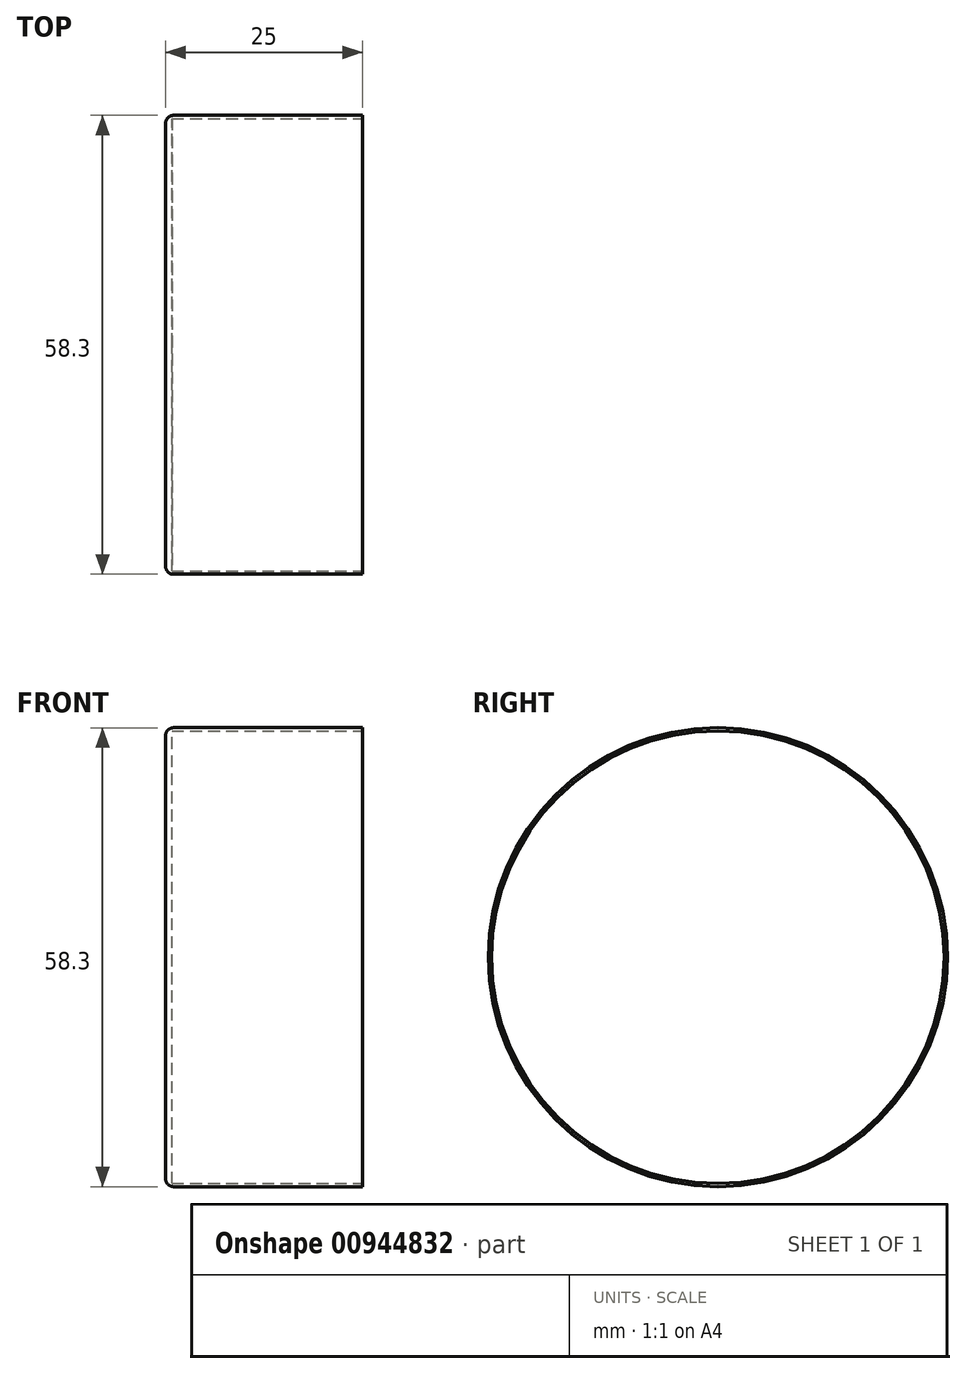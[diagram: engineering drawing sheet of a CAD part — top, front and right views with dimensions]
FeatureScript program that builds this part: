
annotation { "Feature Type Name" : "Feature", "Feature Type Description" : "" }
export const myFeature = defineFeature(function(context is Context, id is Id, definition is map)
    precondition{}
    {
        {
            var Q0;
            Q0=qCreatedBy(makeId("Front.planeOp"),FACE);
            var sketch = newSketch(context, id + "F0", { "sketchPlane" : qUnion([Q0])});
            skLineSegment(sketch, "E0", {"start": v(-31.94, -19.42) * mm, "end": v(-7.94, -19.42) * mm});
            skLineSegment(sketch, "E1", {"start": v(-7.94, -19.42) * mm, "end": v(-7.94, -19.02) * mm});
            skLineSegment(sketch, "E2", {"start": v(-7.94, -19.02) * mm, "end": v(-32.14, -19.02) * mm});
            skLineSegment(sketch, "E3", {"start": v(-32.14, -19.02) * mm, "end": v(-32.14, 9.73) * mm});
            skLineSegment(sketch, "E4", {"start": v(-32.14, 9.73) * mm, "end": v(-32.94, 9.73) * mm});
            skLineSegment(sketch, "E5", {"start": v(-32.94, 9.73) * mm, "end": v(-32.94, -18.42) * mm});
            skPoint(sketch, "E6.visualSharp", {"position": v(-32.94, -19.42) * mm});
            skArc(sketch, "E6.filletArc", {"start": v(-32.94, -18.42) * mm, "mid": v(-32.65, -19.12) * mm, "end": v(-31.94, -19.42) * mm});
            skSolve(sketch);
        }
        {
            var Q0;
            Q0 = qSketchRegion(id + "F0", true);
            var Q1;
            Q1=sQuery(id+"F0.wireOp",EDGE,"E4");
            revolve(context, id + "F1", {"surfaceOperationType" : NewSurfaceOperationType.NEW, "entities" : qUnion([Q0]), "axis" : qUnion([Q1]), "revolveType" : RevolveType.FULL});
        }
    });
